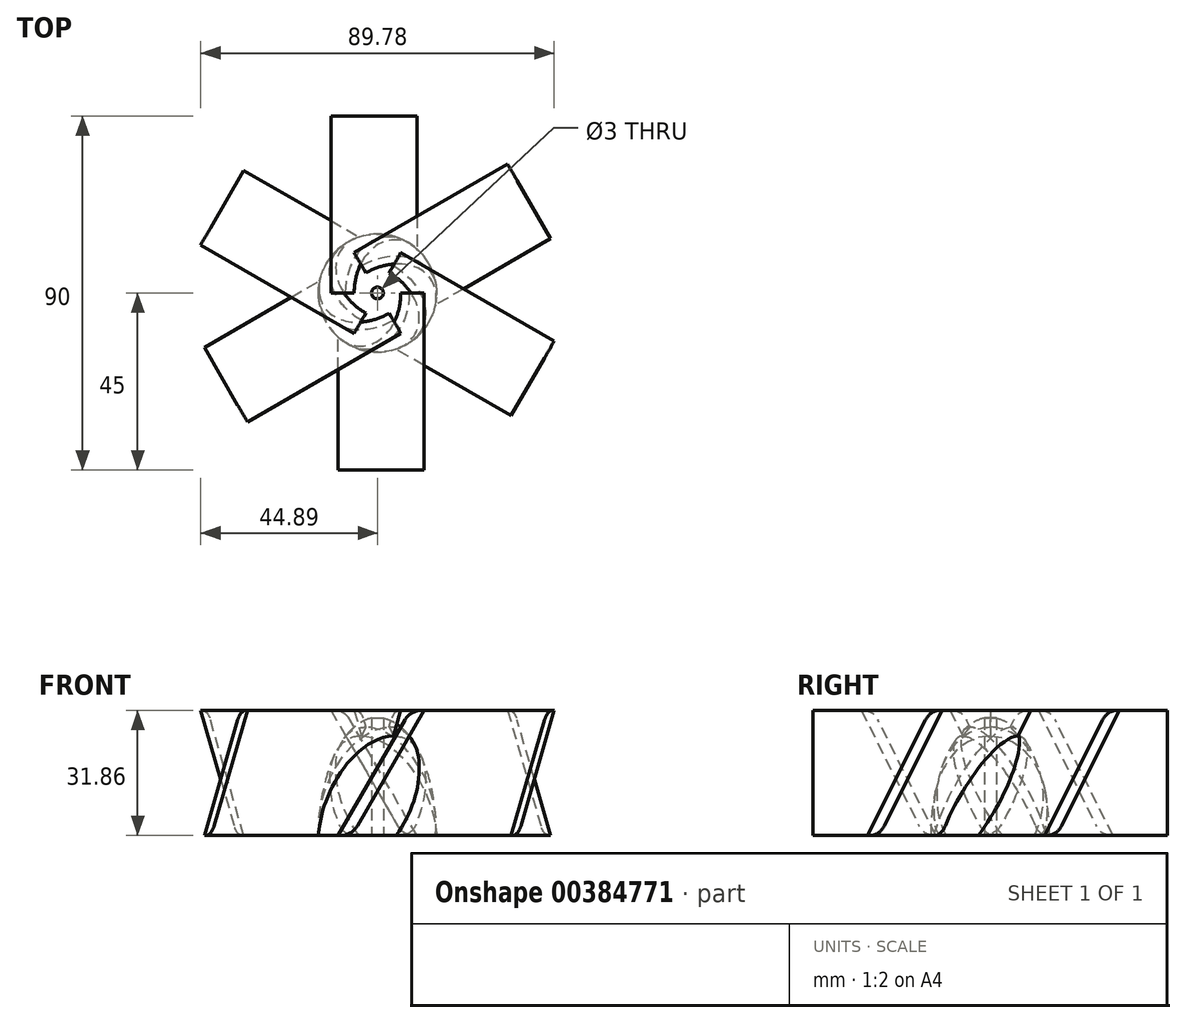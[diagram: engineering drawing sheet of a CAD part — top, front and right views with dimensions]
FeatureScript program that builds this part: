
annotation { "Feature Type Name" : "Feature", "Feature Type Description" : "" }
export const myFeature = defineFeature(function(context is Context, id is Id, definition is map)
    precondition{}
    {
        {
            assignVariable(context, id + "F0", {"name" : "impeller_height", "anyValue" : 50});
        }
        {
            assignVariable(context, id + "F1", {"name" : "impeller_diameter", "anyValue" : 30});
        }
        {
            assignVariable(context, id + "F2", {"name" : "number_of_blades", "anyValue" : 6});
        }
        {
            assignVariable(context, id + "F3", {"name" : "hole_height", "anyValue" : 2 * (getVariable(context, 'impeller_height')) / 3});
        }
        {
            assignVariable(context, id + "F4", {"name" : "blade_lenght", "anyValue" : getVariable(context, 'impeller_diameter') * 1.5});
        }
        {
            var Q0;
            Q0=qCreatedBy(makeId("Front.planeOp"),FACE);
            var sketch = newSketch(context, id + "F5", { "sketchPlane" : qUnion([Q0])});
            skEllipticalArc(sketch, "E0", {});
            skLineSegment(sketch, "E1", {"start": v(-15, 0) * mm, "end": v(15, 0) * mm});
            skLineSegment(sketch, "E2", {"start": v(0, 0) * mm, "end": v(0, 50) * mm});
            const initialGuessF5  = {"E0": [0, 0, 0, 1, 0.03, 0.015, 4.71238898038469, 1.5707963267948966]};
            skSetInitialGuess(sketch, initialGuessF5);
            skSolve(sketch);
        }
        {
            var Q0;
            {var subQ0=sQuery(id+"F5.wireOp",EDGE,"E2");Q0=makeQuery(id+"F5.imprint","IMPRINT",FACE,{"disambiguationData":[TD([[makeQuery(id+"F5.imprint","IMPRINT",EDGE,{"derivedFrom":subQ0}),1.0]])]});}
            var Q1;
            Q1=sQuery(id+"F5.wireOp",EDGE,"E2");
            revolve(context, id + "F6", {"entities" : qUnion([Q0]), "axis" : qUnion([Q1]), "revolveType" : RevolveType.FULL});
        }
        {
            var Q0;
            Q0=qCreatedBy(makeId("Front.planeOp"),FACE);
            var sketch = newSketch(context, id + "F7", { "sketchPlane" : qUnion([Q0])});
            skLineSegment(sketch, "E3", {"start": v(-10, 0) * mm, "end": v(9.25, 33.33) * mm});
            skLineSegment(sketch, "E4", {"start": v(9.25, 33.33) * mm, "end": v(11.84, 31.83) * mm});
            skLineSegment(sketch, "E5", {"start": v(11.84, 31.83) * mm, "end": v(-6.54, 0) * mm});
            skLineSegment(sketch, "E6", {"start": v(-6.54, 0) * mm, "end": v(-10, 0) * mm});
            skSolve(sketch);
        }
        {
            var Q0;
            Q0=qSketchRegion(id+"F7",true);
            extrude(context, id + "F8", {"entities" : qUnion([Q0]), "operationType" : NewBodyOperationType.ADD, "depth" : (getVariable(context, 'blade_lenght')) * mm});
        }
        {
            var Q0;
            Q0=makeQuery(id+"F8.opExtrude","SWEPT_EDGE",EDGE,{"disambiguationData":[OSD([sQuery(id+"F7.wireOp",EDGE,"E3"),sQuery(id+"F7.wireOp",EDGE,"E4")])]});
            var Q1;
            Q1=makeQuery(id+"F8.opExtrude","SWEPT_EDGE",EDGE,{"disambiguationData":[OSD([sQuery(id+"F7.wireOp",EDGE,"E5"),sQuery(id+"F7.wireOp",EDGE,"E6")])]});
            fillet(context, id + "F9", {"entities" : qUnion([Q0, Q1]), "radius" : 5 * mm, "allowEdgeOverflow" : false});
        }
        {
            var Q0;
            Q0=makeQuery(id+"F6.opRevolve","SWEPT_BODY",BODY,{"disambiguationData":[OSD([sQuery(id+"F5.wireOp",EDGE,"E0"),sQuery(id+"F5.wireOp",EDGE,"E1"),sQuery(id+"F5.wireOp",EDGE,"E2")])]});
            var Q1;
            Q1=makeQuery(id+"F6.opRevolve","SWEPT_EDGE",EDGE,{"disambiguationData":[OSD([sQuery(id+"F5.wireOp",EDGE,"E0"),sQuery(id+"F5.wireOp",EDGE,"E1")])]});
            circularPattern(context, id + "F10", {"operationType" : NewBodyOperationType.ADD, "entities" : qUnion([Q0]), "axis" : qUnion([Q1]), "angle" : 360 * degree, "instanceCount" : getVariable(context, 'number_of_blades'), "equalSpace" : true});
        }
        {
            var Q0;
            Q0=makeQuery(id+"F10.opPattern","COPY",FACE,{"derivedFrom":makeQuery(id+"F8.boolean.opBoolean","MERGE",FACE,{"derivedFrom":[makeQuery(id+"F6.opRevolve","SWEPT_FACE",FACE,{"disambiguationData":[OSD([sQuery(id+"F5.wireOp",EDGE,"E1")])]}),makeQuery(id+"F8.opExtrude","SWEPT_FACE",FACE,{"disambiguationData":[OSD([sQuery(id+"F7.wireOp",EDGE,"E6")])]})]}),"instanceName":"3"});
            var sketch = newSketch(context, id + "F11", { "sketchPlane" : qUnion([Q0])});
            skCircle(sketch, "E7", {"center": v(0, 0) * mm, "radius": 1.5 * mm});
            skSolve(sketch);
        }
        {
            var Q0;
            Q0=makeQuery(id+"F11.imprint","IMPRINT",FACE,{"disambiguationData":[TD([[makeQuery(id+"F11.imprint","IMPRINT",EDGE,{"derivedFrom":sQuery(id+"F11.wireOp",EDGE,"E7")}),1.0]])]});
            extrude(context, id + "F12", {"entities" : qUnion([Q0]), "operationType" : NewBodyOperationType.REMOVE, "oppositeDirection" : true, "depth" : (getVariable(context, 'hole_height')) * mm});
        }
    });
